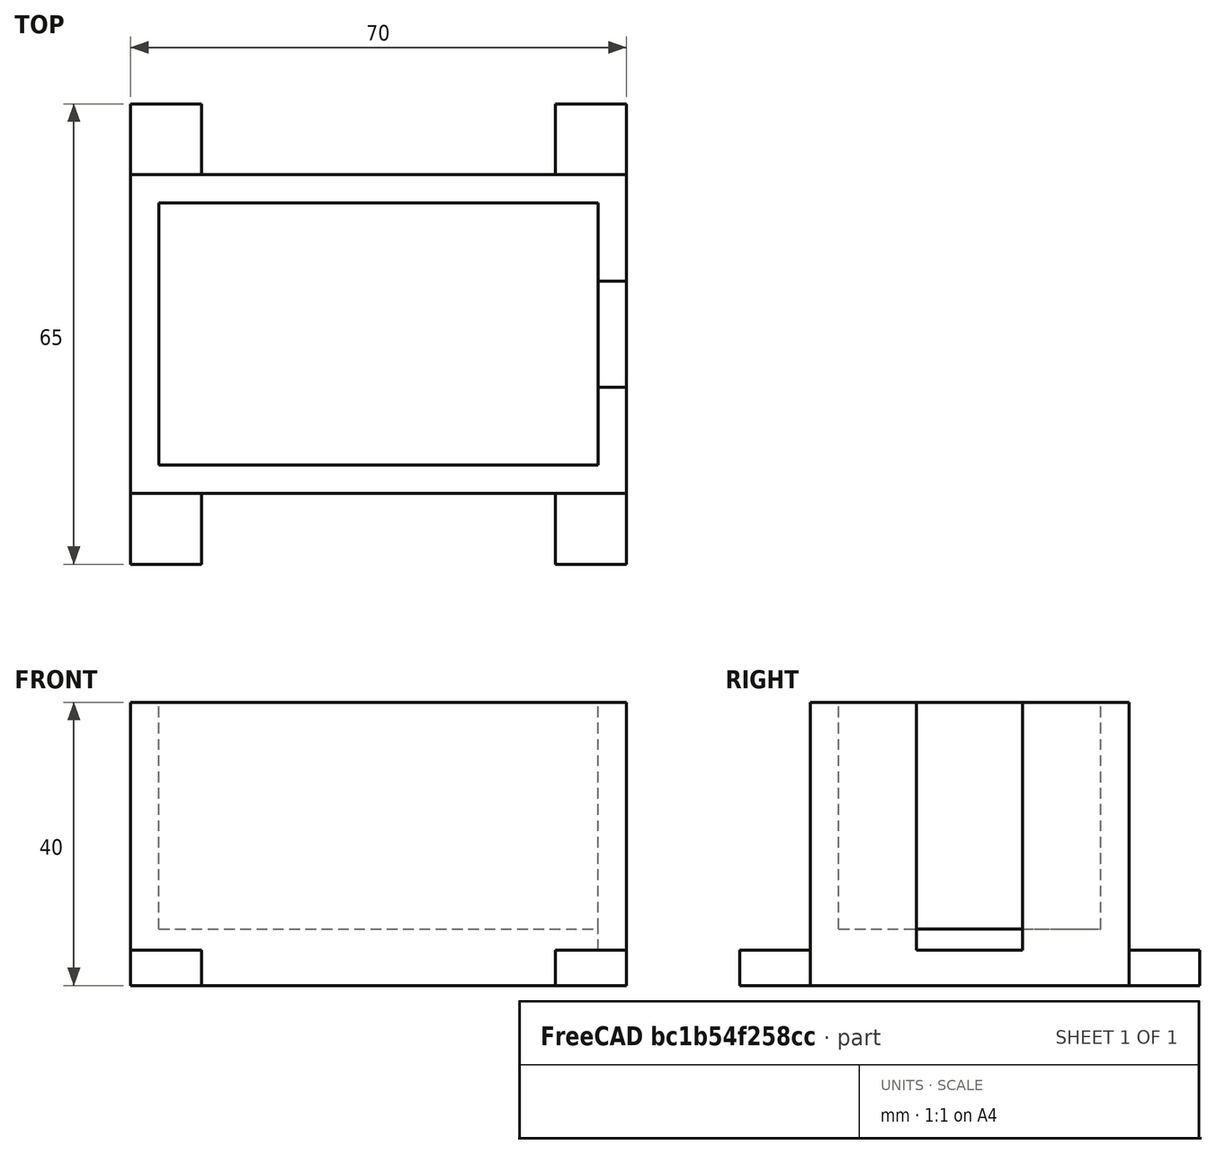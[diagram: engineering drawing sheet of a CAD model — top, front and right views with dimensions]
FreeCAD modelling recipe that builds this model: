
FCSTD DOCUMENT  (FreeCAD 0.14R3702 (Git))
Label: Battery holder
License: CC-BY 3.0
LicenseURL: http://creativecommons.org/licenses/by/3.0/
objects: Part::Box×7, Part::Cut×2
note: 9 computed .brp shape members not serialized (recipe doc carries the construction recipe); baked Part::Feature solids carry a one-line shape summary decoded from their .brp

FEATURE [Part::Box] Box  label="Cube"
  Height = 40
  Length = 70
  Width = 45
FEATURE [Part::Box] Box001  label="Cube001"
  Height = 32
  Length = 62
  Placement = pos=(4,4,8) rot=(0,0,1;0rad)
  Width = 37
FEATURE [Part::Box] Box002  label="Cube002"
  Height = 35
  Length = 4
  Placement = pos=(66,15,5) rot=(0,0,1;0rad)
  Width = 15
FEATURE [Part::Box] Box003  label="Cube003"
  Height = 5
  Length = 10
  Placement = pos=(0,-10,0) rot=(0,0,1;0rad)
  Width = 10
FEATURE [Part::Box] Box004  label="Cube004"
  Height = 5
  Length = 10
  Placement = pos=(60,-10,0) rot=(0,0,1;0rad)
  Width = 10
FEATURE [Part::Box] Box005  label="Cube005"
  Height = 5
  Length = 10
  Placement = pos=(0,45,0) rot=(0,0,1;0rad)
  Width = 10
FEATURE [Part::Box] Box006  label="Cube006"
  Height = 5
  Length = 10
  Placement = pos=(60,45,0) rot=(0,0,1;0rad)
  Width = 10
FEATURE [Part::Cut] Cut
  Base = -> Box
  Tool = -> Box001
FEATURE [Part::Cut] Cut001
  Base = -> Cut
  Tool = -> Box002
